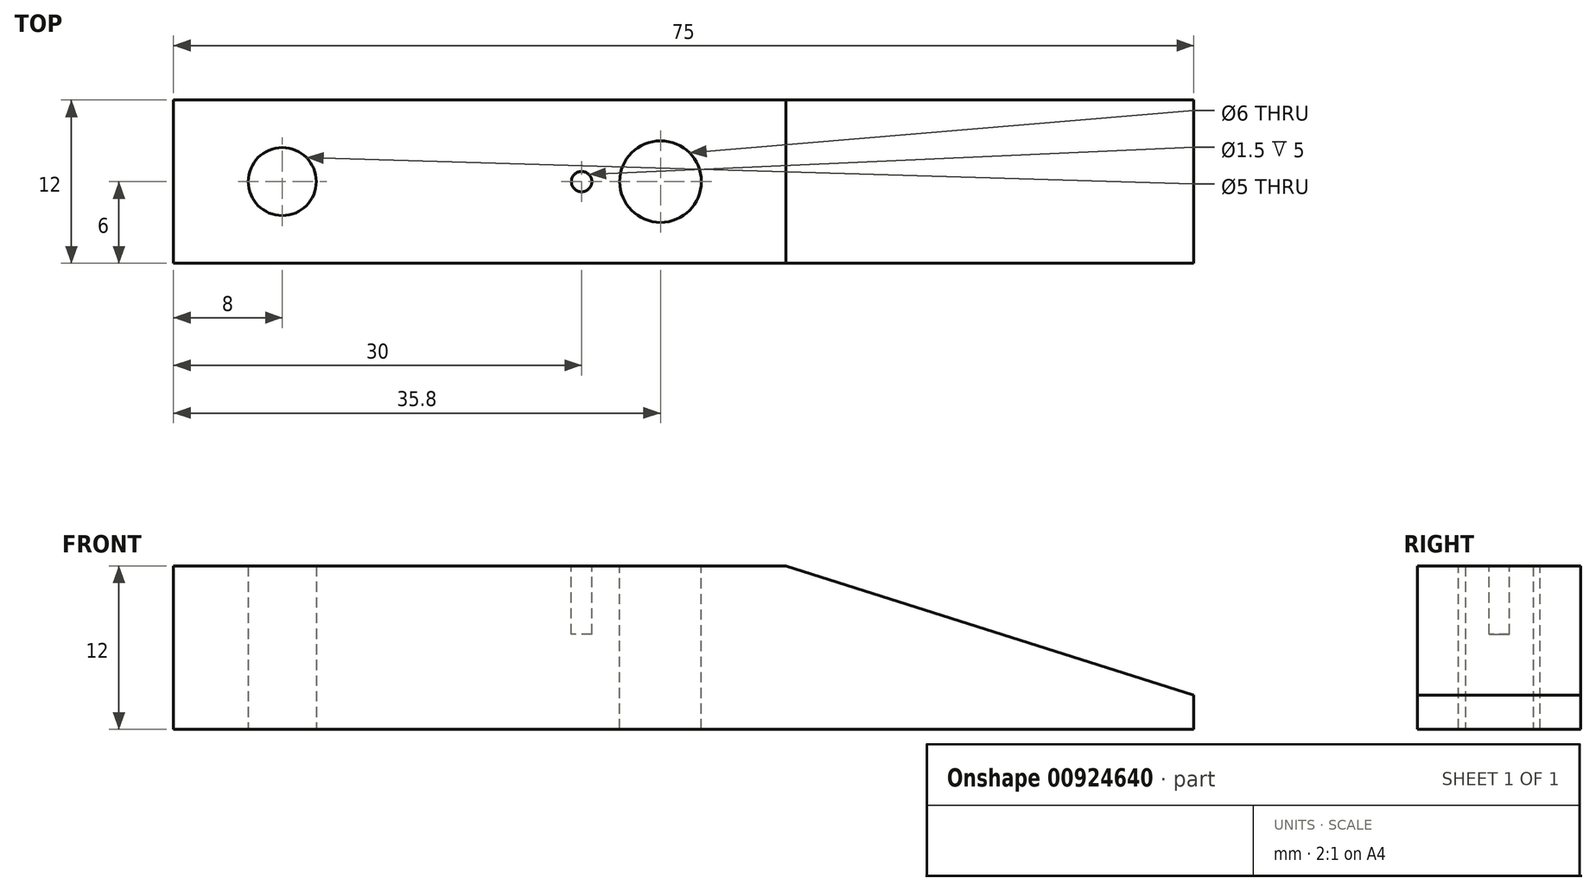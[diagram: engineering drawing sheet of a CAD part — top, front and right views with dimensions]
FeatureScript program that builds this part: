
annotation { "Feature Type Name" : "Feature", "Feature Type Description" : "" }
export const myFeature = defineFeature(function(context is Context, id is Id, definition is map)
    precondition{}
    {
        {
            var Q0;
            Q0=qCreatedBy(makeId("Front.planeOp"),FACE);
            var sketch = newSketch(context, id + "F0", { "sketchPlane" : qUnion([Q0])});
            skLineSegment(sketch, "E0", {"start": v(-35.8, 21.23) * mm, "end": v(-35.8, 9.23) * mm});
            skLineSegment(sketch, "E1", {"start": v(-35.8, 9.23) * mm, "end": v(39.2, 9.23) * mm});
            skLineSegment(sketch, "E2", {"start": v(39.2, 9.23) * mm, "end": v(39.2, 11.73) * mm});
            skLineSegment(sketch, "E3", {"start": v(39.2, 11.73) * mm, "end": v(9.2, 21.23) * mm});
            skLineSegment(sketch, "E4", {"start": v(9.2, 21.23) * mm, "end": v(-35.8, 21.23) * mm});
            skSolve(sketch);
        }
        {
            var Q0;
            Q0=makeQuery(id+"F0.imprint","IMPRINT",FACE,{"disambiguationData":[TD([[makeQuery(id+"F0.imprint","IMPRINT",EDGE,{"derivedFrom":sQuery(id+"F0.wireOp",EDGE,"E0")}),1.0]])]});
            extrude(context, id + "F1", {"entities" : qUnion([Q0]), "oppositeDirection" : true, "depth" : 12 * mm, "offsetDistance" : 25 * mm});
        }
        {
            var Q0;
            Q0=makeQuery(id+"F1.opExtrude","SWEPT_FACE",FACE,{"disambiguationData":[OSD([sQuery(id+"F0.wireOp",EDGE,"E4")])]});
            var sketch = newSketch(context, id + "F2", { "sketchPlane" : qUnion([Q0])});
            skCircle(sketch, "E5", {"center": v(0, 6) * mm, "radius": 3 * mm});
            skSolve(sketch);
        }
        {
            var Q0;
            Q0=qSketchRegion(id+"F2",true);
            extrude(context, id + "F3", {"entities" : qUnion([Q0]), "operationType" : NewBodyOperationType.REMOVE, "endBound" : BoundingType.THROUGH_ALL, "oppositeDirection" : true, "depth" : 25 * mm, "offsetDistance" : 25 * mm});
        }
        {
            var Q0;
            Q0=makeQuery(id+"F1.opExtrude","SWEPT_FACE",FACE,{"disambiguationData":[OSD([sQuery(id+"F0.wireOp",EDGE,"E4")])]});
            var sketch = newSketch(context, id + "F4", { "sketchPlane" : qUnion([Q0])});
            skCircle(sketch, "E6", {"center": v(-5.8, 6) * mm, "radius": 0.75 * mm});
            skSolve(sketch);
        }
        {
            var Q0;
            Q0=qSketchRegion(id+"F4",true);
            extrude(context, id + "F5", {"entities" : qUnion([Q0]), "operationType" : NewBodyOperationType.REMOVE, "oppositeDirection" : true, "depth" : 5 * mm, "offsetDistance" : 25 * mm});
        }
        {
            var Q0;
            Q0=makeQuery(id+"F1.opExtrude","SWEPT_FACE",FACE,{"disambiguationData":[OSD([sQuery(id+"F0.wireOp",EDGE,"E1")])]});
            var sketch = newSketch(context, id + "F6", { "sketchPlane" : qUnion([Q0])});
            skCircle(sketch, "E7", {"center": v(-27.8, -6) * mm, "radius": 2.5 * mm});
            skSolve(sketch);
        }
        {
            var Q0;
            Q0=makeQuery(id+"F6.imprint","IMPRINT",FACE,{"disambiguationData":[TD([[makeQuery(id+"F6.imprint","IMPRINT",EDGE,{"derivedFrom":sQuery(id+"F6.wireOp",EDGE,"E7")}),1.0]])]});
            extrude(context, id + "F7", {"entities" : qUnion([Q0]), "operationType" : NewBodyOperationType.REMOVE, "endBound" : BoundingType.THROUGH_ALL, "oppositeDirection" : true, "depth" : 25 * mm, "offsetDistance" : 25 * mm});
        }
    });
